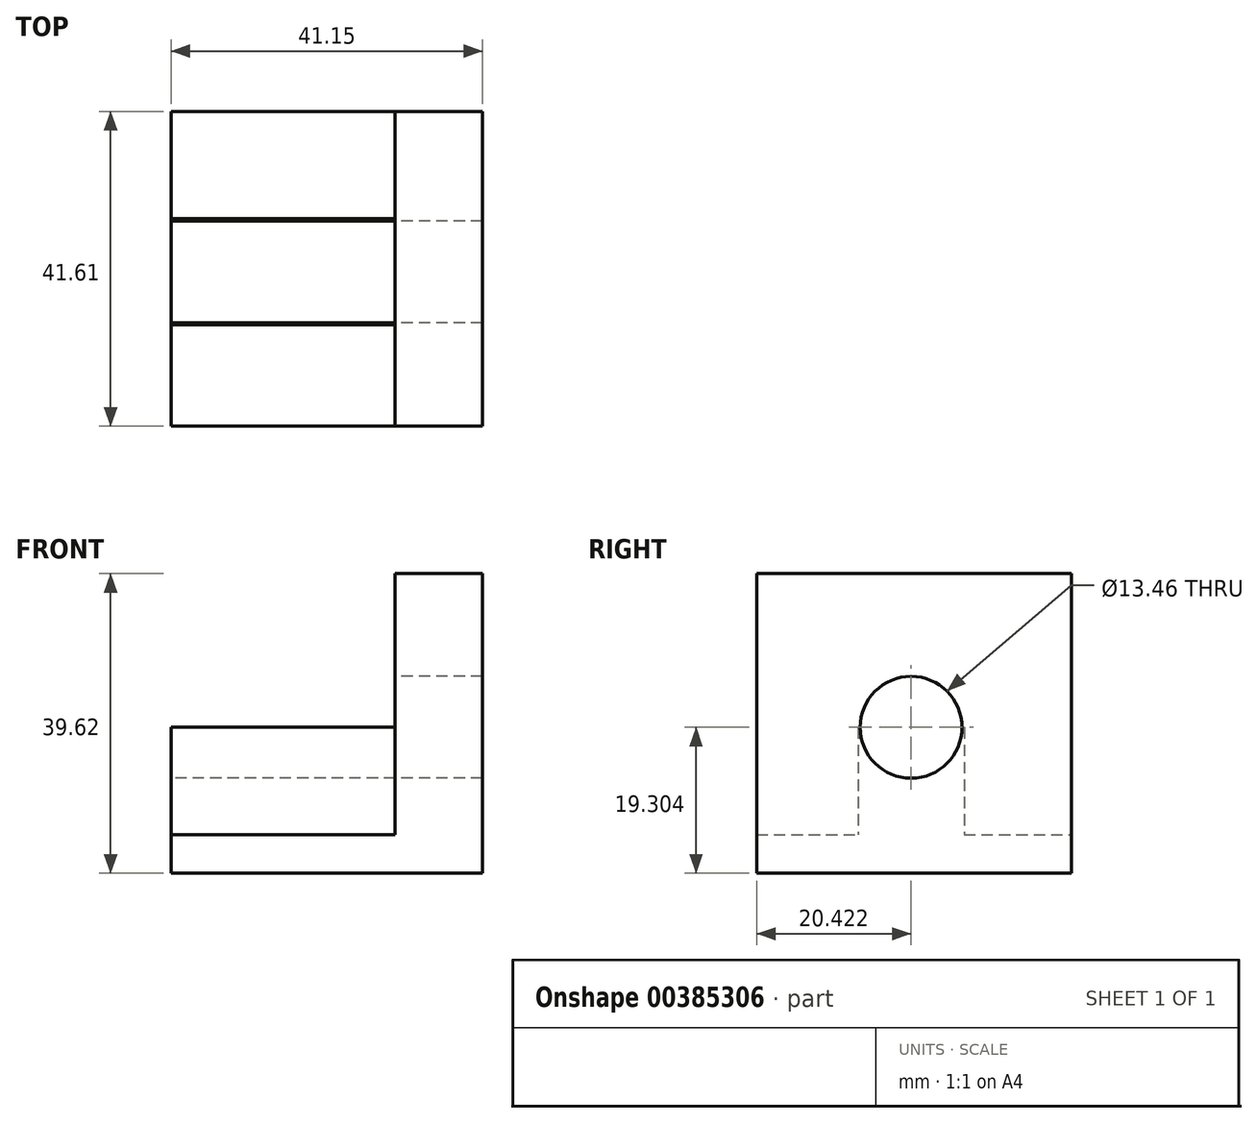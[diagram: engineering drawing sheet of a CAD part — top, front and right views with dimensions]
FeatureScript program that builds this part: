
annotation { "Feature Type Name" : "Feature", "Feature Type Description" : "" }
export const myFeature = defineFeature(function(context is Context, id is Id, definition is map)
    precondition{}
    {
        {
            var Q0;
            Q0=qCreatedBy(makeId("Top.planeOp"),FACE);
            var sketch = newSketch(context, id + "F0", { "sketchPlane" : qUnion([Q0])});
            skLineSegment(sketch, "E0.bottom", {"start": v(0, 0) * mm, "end": v(-41.15, 0) * mm});
            skLineSegment(sketch, "E0.top", {"start": v(0, 41.6) * mm, "end": v(-41.15, 41.6) * mm});
            skLineSegment(sketch, "E0.left", {"start": v(0, 0) * mm, "end": v(0, 41.6) * mm});
            skLineSegment(sketch, "E0.right", {"start": v(-41.15, 0) * mm, "end": v(-41.15, 41.6) * mm});
            skSolve(sketch);
        }
        {
            var Q0;
            Q0 = qSketchRegion(id + "F0", true);
            extrude(context, id + "F1", {"entities" : qUnion([Q0]), "depth" : 5.08 * mm});
        }
        {
            var Q0;
            Q0=makeQuery(id+"F1.opExtrude","CAP_FACE",FACE,{"disambiguationData":[OSD([sQuery(id+"F0.wireOp",EDGE,"E0.bottom"),sQuery(id+"F0.wireOp",EDGE,"E0.top"),sQuery(id+"F0.wireOp",EDGE,"E0.left"),sQuery(id+"F0.wireOp",EDGE,"E0.right")])],"isStart":false});
            var sketch = newSketch(context, id + "F2", { "sketchPlane" : qUnion([Q0])});
            skLineSegment(sketch, "E1.bottom", {"start": v(0, 41.6) * mm, "end": v(-11.58, 41.6) * mm});
            skLineSegment(sketch, "E1.top", {"start": v(0, 0) * mm, "end": v(-11.58, 0) * mm});
            skLineSegment(sketch, "E1.left", {"start": v(0, 41.6) * mm, "end": v(0, 0) * mm});
            skLineSegment(sketch, "E1.right", {"start": v(-11.58, 41.6) * mm, "end": v(-11.58, 0) * mm});
            skSolve(sketch);
        }
        {
            var Q0;
            Q0 = qSketchRegion(id + "F2", true);
            extrude(context, id + "F3", {"entities" : qUnion([Q0]), "operationType" : NewBodyOperationType.ADD, "depth" : 34.54 * mm});
        }
        {
            var Q0;
            Q0=makeQuery(id+"F1.opExtrude","CAP_FACE",FACE,{"disambiguationData":[OSD([sQuery(id+"F0.wireOp",EDGE,"E0.bottom"),sQuery(id+"F0.wireOp",EDGE,"E0.top"),sQuery(id+"F0.wireOp",EDGE,"E0.left"),sQuery(id+"F0.wireOp",EDGE,"E0.right")])],"isStart":false});
            var sketch = newSketch(context, id + "F4", { "sketchPlane" : qUnion([Q0])});
            skLineSegment(sketch, "E2.bottom", {"start": v(-11.58, 27.43) * mm, "end": v(-41.15, 27.43) * mm});
            skLineSegment(sketch, "E2.top", {"start": v(-11.58, 13.41) * mm, "end": v(-41.15, 13.41) * mm});
            skLineSegment(sketch, "E2.left", {"start": v(-11.58, 27.43) * mm, "end": v(-11.58, 13.41) * mm});
            skLineSegment(sketch, "E2.right", {"start": v(-41.15, 27.43) * mm, "end": v(-41.15, 13.41) * mm});
            skSolve(sketch);
        }
        {
            var Q0;
            Q0=makeQuery(id+"F4.imprint","IMPRINT",FACE,{"disambiguationData":[TD([[makeQuery(id+"F4.imprint","IMPRINT",EDGE,{"derivedFrom":sQuery(id+"F4.wireOp",EDGE,"E2.bottom")}),1.0]])]});
            extrude(context, id + "F5", {"entities" : qUnion([Q0]), "operationType" : NewBodyOperationType.ADD, "depth" : 14.22 * mm});
        }
        {
            var Q0;
            Q0=makeQuery(id+"F5.boolean.opBoolean","MERGE",FACE,{"derivedFrom":[makeQuery(id+"F1.opExtrude","SWEPT_FACE",FACE,{"disambiguationData":[OSD([sQuery(id+"F0.wireOp",EDGE,"E0.right")])]}),makeQuery(id+"F5.opExtrude","SWEPT_FACE",FACE,{"disambiguationData":[OSD([sQuery(id+"F4.wireOp",EDGE,"E2.right")])]})]});
            var sketch = newSketch(context, id + "F6", { "sketchPlane" : qUnion([Q0])});
            skPoint(sketch, "E3", {"position": v(-20.42, 19.3) * mm});
            skSolve(sketch);
        }
        {
            var Q0;
            Q0=sQuery(id+"F6.wireOp",VERTEX,"E3");
            var Q1;
            Q1=makeQuery(id+"F1.opExtrude","SWEPT_BODY",BODY,{"disambiguationData":[OSD([sQuery(id+"F0.wireOp",EDGE,"E0.bottom"),sQuery(id+"F0.wireOp",EDGE,"E0.top"),sQuery(id+"F0.wireOp",EDGE,"E0.left"),sQuery(id+"F0.wireOp",EDGE,"E0.right")])]});
            hole(context, id + "F7", {"style" : HoleStyle.SIMPLE, "endStyle" : HoleEndStyle.THROUGH, "holeDiameter" : 13.46 * mm, "isTappedThrough" : true, "tappedDepth" : 12.7 * mm, "tapClearance" : 3, "locations" : qUnion([Q0]), "scope" : qUnion([Q1])});
        }
    });
